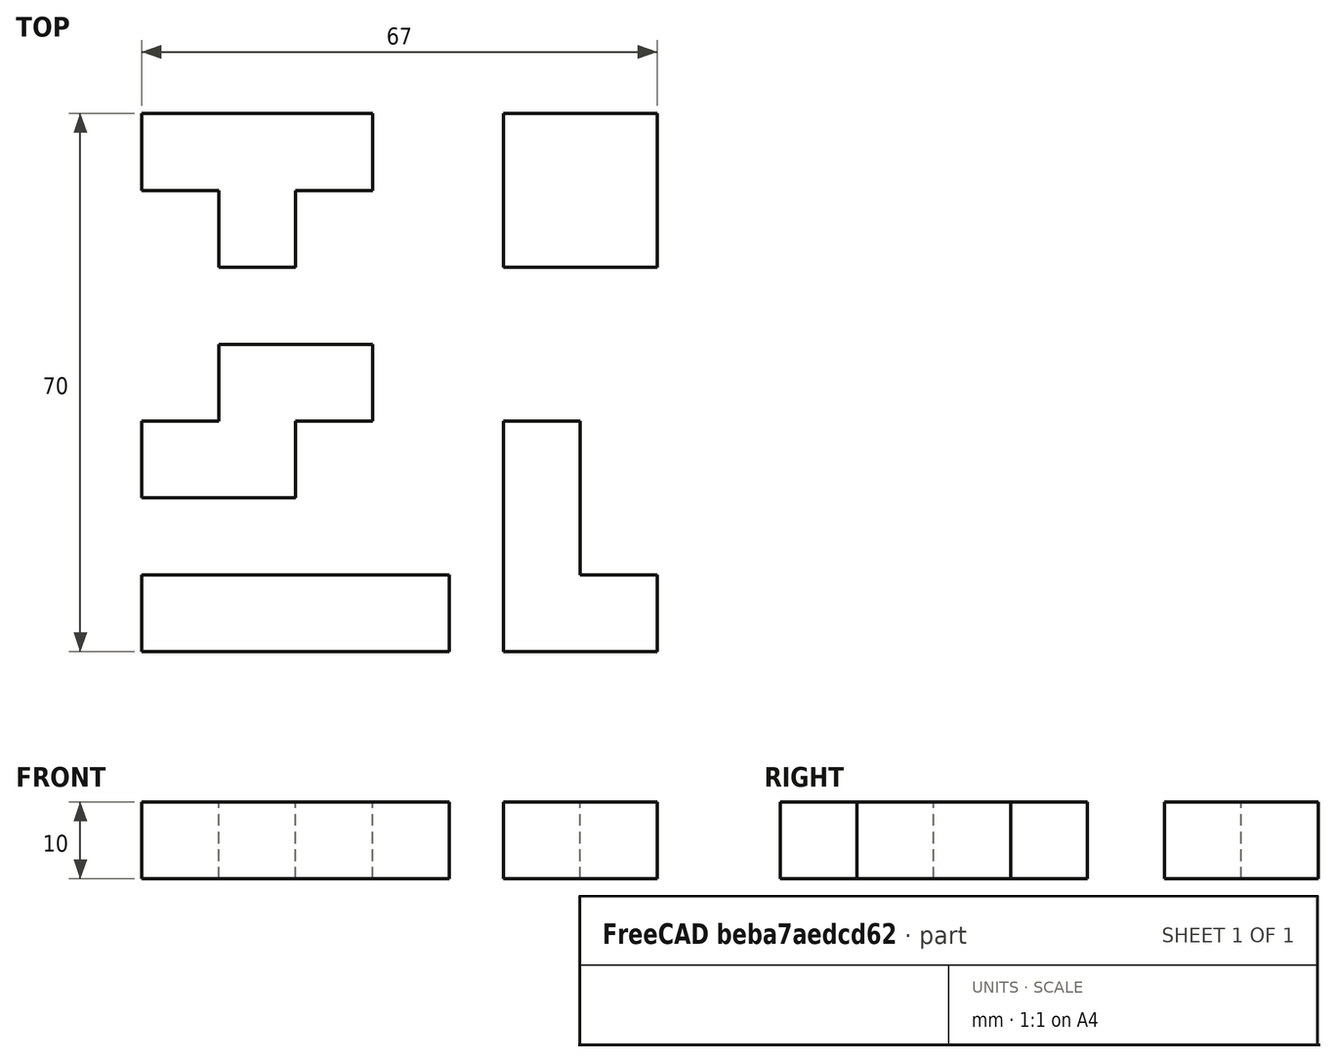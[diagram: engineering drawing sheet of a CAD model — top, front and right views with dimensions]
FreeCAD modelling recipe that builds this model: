
FCSTD DOCUMENT  (FreeCAD 0.21R33771 (Git))
Label: OJT1_T05R03_unions_tetris
License: All rights reserved
LicenseURL: https://en.wikipedia.org/wiki/All_rights_reserved
objects: Part::Box×20, Part::MultiFuse×5
note: 25 computed .brp shape members not serialized (recipe doc carries the construction recipe); baked Part::Feature solids carry a one-line shape summary decoded from their .brp

FEATURE [Part::Box] Box  label="Cube"
  AttacherType = Attacher::AttachEngine3D
  Height = 10
  Length = 10
  Width = 10
FEATURE [Part::Box] Box001  label="Cube001"
  AttacherType = Attacher::AttachEngine3D
  Height = 10
  Length = 10
  Placement = pos=(10,0,0) rot=(0,0,1;0rad)
  Width = 10
FEATURE [Part::Box] Box002  label="Cube002"
  AttacherType = Attacher::AttachEngine3D
  Height = 10
  Length = 10
  Placement = pos=(20,0,0) rot=(0,0,1;0rad)
  Width = 10
FEATURE [Part::Box] Box003  label="Cube003"
  AttacherType = Attacher::AttachEngine3D
  Height = 10
  Length = 10
  Placement = pos=(30,0,0) rot=(0,0,1;0rad)
  Width = 10
FEATURE [Part::MultiFuse] Fusion  label="vermell"
  Refine = true
  Shapes = -> [Box,Box001,Box002,Box003]
FEATURE [Part::Box] Box004  label="Cube004"
  AttacherType = Attacher::AttachEngine3D
  Height = 10
  Length = 10
  Placement = pos=(47,0,0) rot=(0,0,1;0rad)
  Width = 10
FEATURE [Part::Box] Box005  label="Cube005"
  AttacherType = Attacher::AttachEngine3D
  Height = 10
  Length = 10
  Placement = pos=(57,0,0) rot=(0,0,1;0rad)
  Width = 10
FEATURE [Part::Box] Box006  label="Cube006"
  AttacherType = Attacher::AttachEngine3D
  Height = 10
  Length = 10
  Placement = pos=(47,10,0) rot=(0,0,1;0rad)
  Width = 10
FEATURE [Part::Box] Box007  label="Cube007"
  AttacherType = Attacher::AttachEngine3D
  Height = 10
  Length = 10
  Placement = pos=(47,20,0) rot=(0,0,1;0rad)
  Width = 10
FEATURE [Part::MultiFuse] Fusion001  label="groc"
  Refine = true
  Shapes = -> [Box004,Box005,Box006,Box007]
FEATURE [Part::Box] Box008  label="Cube008"
  AttacherType = Attacher::AttachEngine3D
  Height = 10
  Length = 10
  Placement = pos=(0,20,0) rot=(0,0,1;0rad)
  Width = 10
FEATURE [Part::Box] Box009  label="Cube009"
  AttacherType = Attacher::AttachEngine3D
  Height = 10
  Length = 10
  Placement = pos=(10,20,0) rot=(0,0,1;0rad)
  Width = 10
FEATURE [Part::Box] Box010  label="Cube010"
  AttacherType = Attacher::AttachEngine3D
  Height = 10
  Length = 10
  Placement = pos=(10,30,0) rot=(0,0,1;0rad)
  Width = 10
FEATURE [Part::Box] Box011  label="Cube011"
  AttacherType = Attacher::AttachEngine3D
  Height = 10
  Length = 10
  Placement = pos=(20,30,0) rot=(0,0,1;0rad)
  Width = 10
FEATURE [Part::MultiFuse] Fusion002  label="blau"
  Refine = true
  Shapes = -> [Box008,Box009,Box010,Box011]
FEATURE [Part::Box] Box012  label="Cube012"
  AttacherType = Attacher::AttachEngine3D
  Height = 10
  Length = 10
  Placement = pos=(10,50,0) rot=(0,0,1;0rad)
  Width = 10
FEATURE [Part::Box] Box013  label="Cube013"
  AttacherType = Attacher::AttachEngine3D
  Height = 10
  Length = 10
  Placement = pos=(0,60,0) rot=(0,0,1;0rad)
  Width = 10
FEATURE [Part::Box] Box014  label="Cube014"
  AttacherType = Attacher::AttachEngine3D
  Height = 10
  Length = 10
  Placement = pos=(10,60,0) rot=(0,0,1;0rad)
  Width = 10
FEATURE [Part::Box] Box015  label="Cube015"
  AttacherType = Attacher::AttachEngine3D
  Height = 10
  Length = 10
  Placement = pos=(20,60,0) rot=(0,0,1;0rad)
  Width = 10
FEATURE [Part::MultiFuse] Fusion003  label="gris"
  Refine = true
  Shapes = -> [Box012,Box013,Box014,Box015]
FEATURE [Part::Box] Box016  label="Cube016"
  AttacherType = Attacher::AttachEngine3D
  Height = 10
  Length = 10
  Placement = pos=(47,60,0) rot=(0,0,1;0rad)
  Width = 10
FEATURE [Part::Box] Box017  label="Cube017"
  AttacherType = Attacher::AttachEngine3D
  Height = 10
  Length = 10
  Placement = pos=(47,50,0) rot=(0,0,1;0rad)
  Width = 10
FEATURE [Part::Box] Box018  label="Cube018"
  AttacherType = Attacher::AttachEngine3D
  Height = 10
  Length = 10
  Placement = pos=(57,60,0) rot=(0,0,1;0rad)
  Width = 10
FEATURE [Part::Box] Box019  label="Cube019"
  AttacherType = Attacher::AttachEngine3D
  Height = 10
  Length = 10
  Placement = pos=(57,50,0) rot=(0,0,1;0rad)
  Width = 10
FEATURE [Part::MultiFuse] Fusion004  label="blau_cel"
  Refine = true
  Shapes = -> [Box016,Box017,Box018,Box019]
